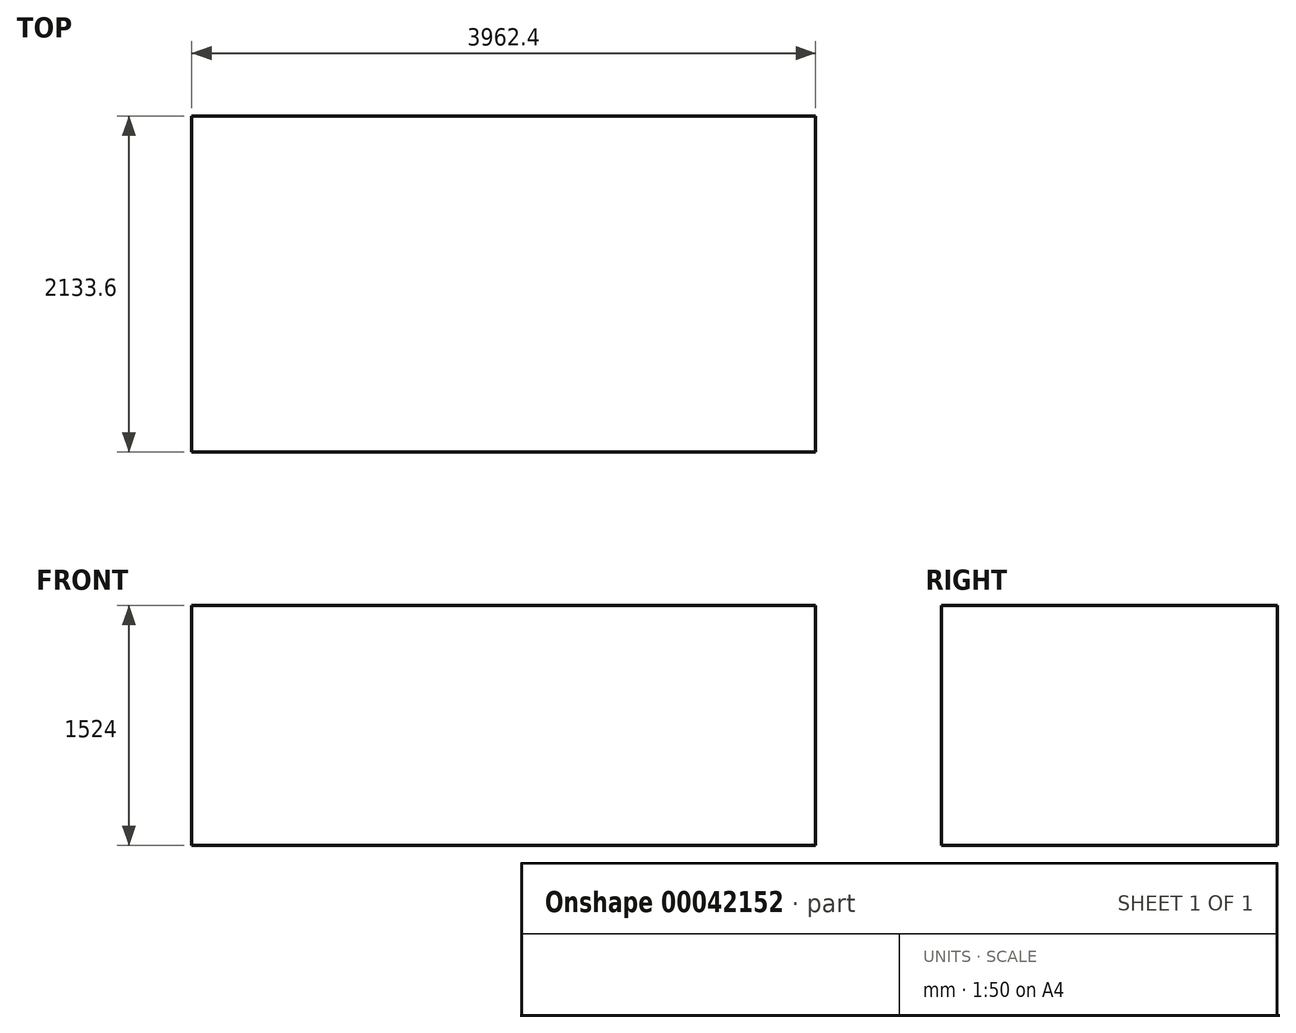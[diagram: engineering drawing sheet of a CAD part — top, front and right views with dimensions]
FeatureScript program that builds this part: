
annotation { "Feature Type Name" : "Feature", "Feature Type Description" : "" }
export const myFeature = defineFeature(function(context is Context, id is Id, definition is map)
    precondition{}
    {
        {
            var Q0;
            Q0=qCreatedBy(makeId("Top.planeOp"),FACE);
            var sketch = newSketch(context, id + "F0", { "sketchPlane" : qUnion([Q0])});
            skLineSegment(sketch, "E0.bottom", {"start": v(0, 0) * mm, "end": v(3962.4, 0) * mm});
            skLineSegment(sketch, "E0.top", {"start": v(0, 2133.6) * mm, "end": v(3962.4, 2133.6) * mm});
            skLineSegment(sketch, "E0.left", {"start": v(0, 0) * mm, "end": v(0, 2133.6) * mm});
            skLineSegment(sketch, "E0.right", {"start": v(3962.4, 0) * mm, "end": v(3962.4, 2133.6) * mm});
            skSolve(sketch);
        }
        {
            var Q0;
            Q0 = qSketchRegion(id + "F0", true);
            extrude(context, id + "F1", {"entities" : qUnion([Q0]), "depth" : 1524 * mm});
        }
    });
